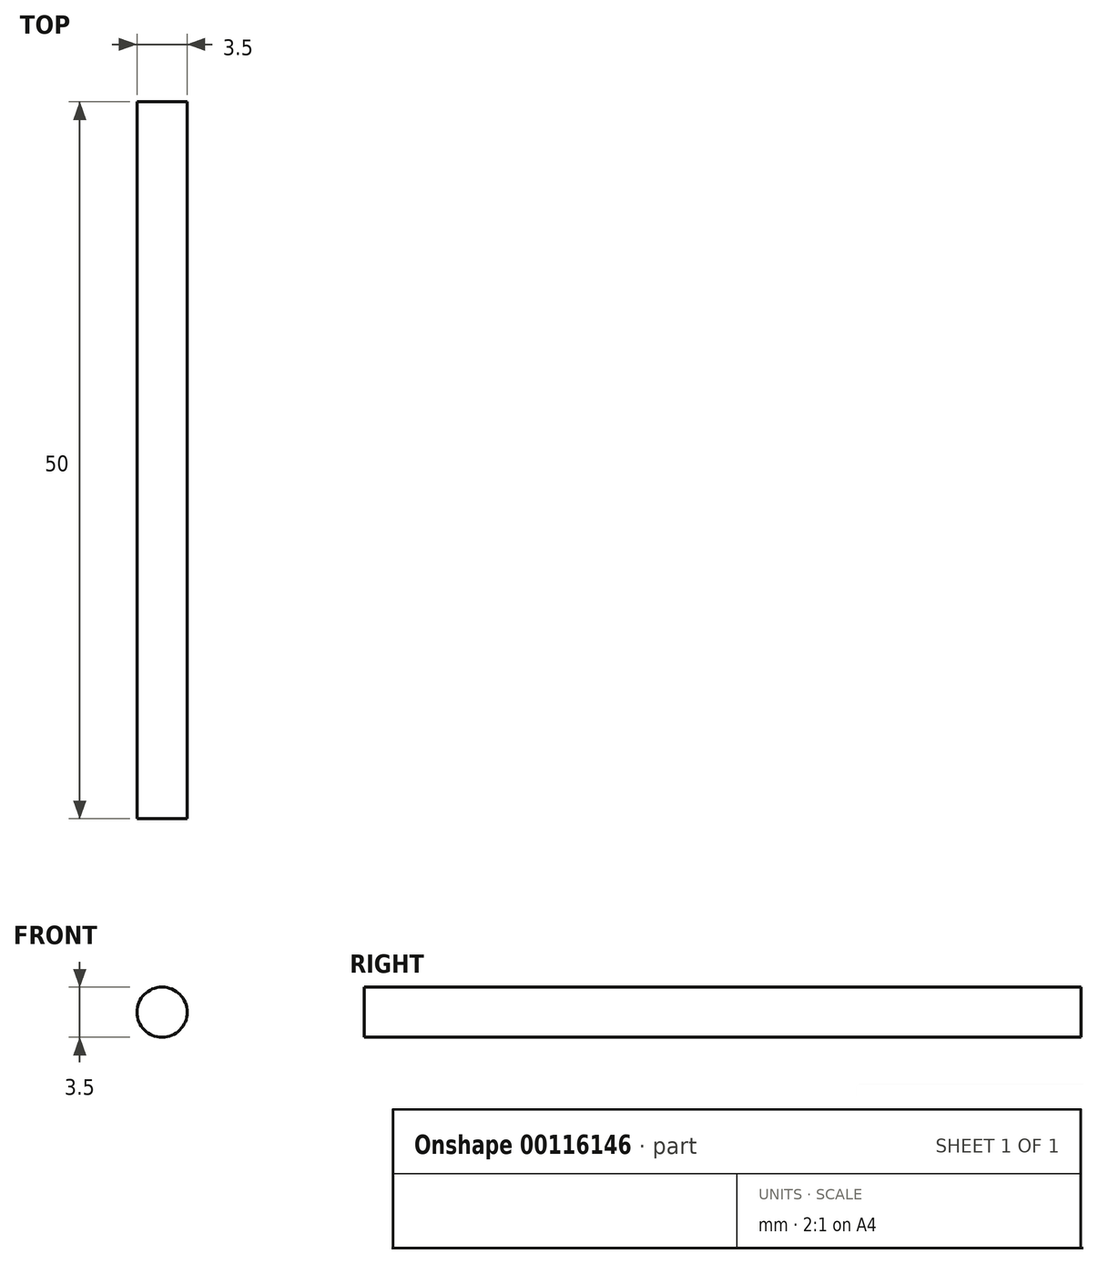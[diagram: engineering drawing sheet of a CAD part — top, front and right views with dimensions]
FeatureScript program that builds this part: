
annotation { "Feature Type Name" : "Feature", "Feature Type Description" : "" }
export const myFeature = defineFeature(function(context is Context, id is Id, definition is map)
    precondition{}
    {
        {
            var Q0;
            Q0=qCreatedBy(makeId("Front.planeOp"),FACE);
            var sketch = newSketch(context, id + "F0", { "sketchPlane" : qUnion([Q0])});
            skCircle(sketch, "E0", {"center": v(0, 0) * mm, "radius": 1.75 * mm});
            skSolve(sketch);
        }
        {
            var Q0;
            Q0=makeQuery(id+"F0.imprint","IMPRINT",FACE,{"disambiguationData":[TD([[makeQuery(id+"F0.imprint","IMPRINT",EDGE,{"derivedFrom":sQuery(id+"F0.wireOp",EDGE,"E0")}),1.0]])]});
            extrude(context, id + "F1", {"entities" : qUnion([Q0]), "depth" : 50 * mm});
        }
    });
